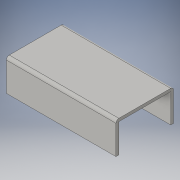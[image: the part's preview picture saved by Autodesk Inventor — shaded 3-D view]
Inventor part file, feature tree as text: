
AUTODESK INVENTOR PART (.ipt)
format: ipt  version: 2016 (Build 200138000, 138)  size: 110,592 bytes
history: native  units: in
note: dims shown in document units (in); Inventor stores cm internally (conversion verified against a paired STEP export)
features: extrude x3, sketch x3, fillet x2
ambient origin geometry x8: Origin, YZ Plane, XZ Plane, XY Plane, X Axis, Y Axis, Z Axis, Center Point
bodies: Solid1 (feature_tree)
feature tree (8):
  extrude  "Extrusion1"  Depth=2.5in
  extrude  "Extrusion2"  Depth=1.25in
  extrude  "Extrusion4"  Depth=0.125in TaperAngle=0.0deg
  fillet  "Fillet1"  Radius=0.125in
  fillet  "Fillet2"  Radius=0.125in
  sketch  "Sketch1"  dims[d0=4.75in d1=2.5in]
  sketch  "Sketch2"  dims[d2=0.125in d3=0.0in d4=1.25in]
  sketch  "Sketch4"  dims[d5=0.125in d6=0.0in d9=0.125in d10=0.0in d11=0.125in d12=0.125in]
